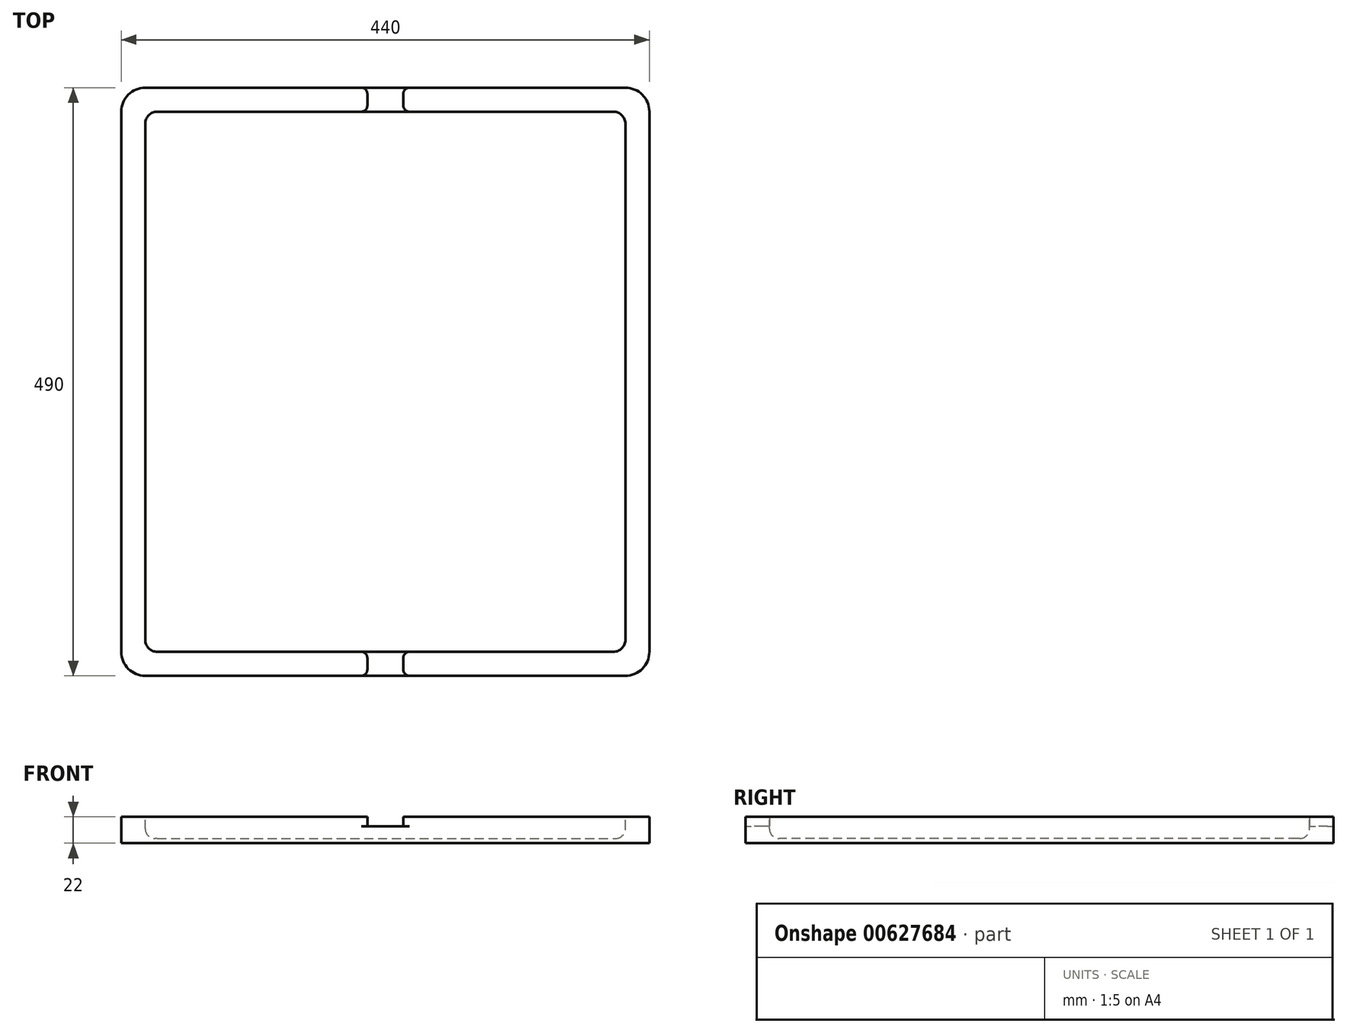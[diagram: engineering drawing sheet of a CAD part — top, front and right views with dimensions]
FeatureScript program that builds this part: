
annotation { "Feature Type Name" : "Feature", "Feature Type Description" : "" }
export const myFeature = defineFeature(function(context is Context, id is Id, definition is map)
    precondition{}
    {
        {
            var Q0;
            Q0=qCreatedBy(makeId("Top.planeOp"),FACE);
            var sketch = newSketch(context, id + "F0", { "sketchPlane" : qUnion([Q0])});
            skLineSegment(sketch, "E0", {"start": v(0, 245) * mm, "end": v(-200, 245) * mm});
            skLineSegment(sketch, "E1", {"start": v(-220, 225) * mm, "end": v(-220, 0) * mm});
            skArc(sketch, "E2", {"start": v(-200, 245) * mm, "mid": v(-214.14, 239.14) * mm, "end": v(-220, 225) * mm});
            skLineSegment(sketch, "E3.MirrorCS", {"start": v(220, 225) * mm, "end": v(220, 0) * mm});
            skArc(sketch, "E4.MirrorCS", {"start": v(200, 245) * mm, "mid": v(214.14, 239.14) * mm, "end": v(220, 225) * mm});
            skLineSegment(sketch, "E5.MirrorCS", {"start": v(0, 245) * mm, "end": v(200, 245) * mm});
            skLineSegment(sketch, "E6.MirrorCS", {"start": v(-220, -225) * mm, "end": v(-220, 0) * mm});
            skArc(sketch, "E7.MirrorCS", {"start": v(-200, -245) * mm, "mid": v(-214.14, -239.14) * mm, "end": v(-220, -225) * mm});
            skLineSegment(sketch, "E8.MirrorCS", {"start": v(0, -245) * mm, "end": v(-200, -245) * mm});
            skLineSegment(sketch, "E9.MirrorCS", {"start": v(0, -245) * mm, "end": v(200, -245) * mm});
            skArc(sketch, "E10.MirrorCS", {"start": v(200, -245) * mm, "mid": v(214.14, -239.14) * mm, "end": v(220, -225) * mm});
            skLineSegment(sketch, "E11.MirrorCS", {"start": v(220, -225) * mm, "end": v(220, 0) * mm});
            skSolve(sketch);
        }
        {
            var Q0;
            Q0=makeQuery(id+"F0.imprint","IMPRINT",FACE,{"disambiguationData":[TD([[makeQuery(id+"F0.imprint","IMPRINT",EDGE,{"derivedFrom":sQuery(id+"F0.wireOp",EDGE,"E0")}),1.0]])]});
            extrude(context, id + "F1", {"entities" : qUnion([Q0]), "depth" : 22 * mm, "offsetDistance" : 25 * mm});
        }
        {
            var Q0;
            Q0=makeQuery(id+"F1.opExtrude","CAP_FACE",FACE,{"disambiguationData":[OSD([sQuery(id+"F0.wireOp",EDGE,"E0"),sQuery(id+"F0.wireOp",EDGE,"E1"),sQuery(id+"F0.wireOp",EDGE,"E2"),sQuery(id+"F0.wireOp",EDGE,"E3.MirrorCS"),sQuery(id+"F0.wireOp",EDGE,"E4.MirrorCS"),sQuery(id+"F0.wireOp",EDGE,"E5.MirrorCS"),sQuery(id+"F0.wireOp",EDGE,"E6.MirrorCS"),sQuery(id+"F0.wireOp",EDGE,"E7.MirrorCS"),sQuery(id+"F0.wireOp",EDGE,"E8.MirrorCS"),sQuery(id+"F0.wireOp",EDGE,"E9.MirrorCS"),sQuery(id+"F0.wireOp",EDGE,"E10.MirrorCS"),sQuery(id+"F0.wireOp",EDGE,"E11.MirrorCS")])],"isStart":false});
            var sketch = newSketch(context, id + "F2", { "sketchPlane" : qUnion([Q0])});
            skLineSegment(sketch, "E12.bottom", {"start": v(-190, 225) * mm, "end": v(190, 225) * mm});
            skLineSegment(sketch, "E12.top", {"start": v(-190, -225) * mm, "end": v(190, -225) * mm});
            skLineSegment(sketch, "E12.left", {"start": v(-200, 215) * mm, "end": v(-200, -215) * mm});
            skLineSegment(sketch, "E12.right", {"start": v(200, 215) * mm, "end": v(200, -215) * mm});
            skPoint(sketch, "E13.visualSharp", {"position": v(200, -225) * mm});
            skArc(sketch, "E13.filletArc", {"start": v(190, -225) * mm, "mid": v(197.07, -222.07) * mm, "end": v(200, -215) * mm});
            skPoint(sketch, "E14.visualSharp", {"position": v(-200, -225) * mm});
            skArc(sketch, "E14.filletArc", {"start": v(-200, -215) * mm, "mid": v(-197.07, -222.07) * mm, "end": v(-190, -225) * mm});
            skPoint(sketch, "E15.visualSharp", {"position": v(-200, 225) * mm});
            skArc(sketch, "E15.filletArc", {"start": v(-190, 225) * mm, "mid": v(-197.07, 222.07) * mm, "end": v(-200, 215) * mm});
            skPoint(sketch, "E16.visualSharp", {"position": v(200, 225) * mm});
            skArc(sketch, "E16.filletArc", {"start": v(200, 215) * mm, "mid": v(197.07, 222.07) * mm, "end": v(190, 225) * mm});
            skSolve(sketch);
        }
        {
            var Q0;
            Q0=makeQuery(id+"F2.imprint","IMPRINT",FACE,{"disambiguationData":[TD([[makeQuery(id+"F2.imprint","IMPRINT",EDGE,{"derivedFrom":sQuery(id+"F2.wireOp",EDGE,"E12.bottom")}),-1.0]])]});
            extrude(context, id + "F3", {"entities" : qUnion([Q0]), "operationType" : NewBodyOperationType.REMOVE, "oppositeDirection" : true, "depth" : 18 * mm, "offsetDistance" : 25 * mm});
        }
        {
            var Q0;
            Q0=makeQuery(id+"F3.boolean.opBoolean","COPY",EDGE,{"derivedFrom":makeQuery(id+"F3.opExtrude","CAP_EDGE",EDGE,{"disambiguationData":[OSD([sQuery(id+"F2.wireOp",EDGE,"E12.bottom")])],"isStart":false})});
            var Q1;
            Q1=makeQuery(id+"F3.boolean.opBoolean","COPY",EDGE,{"derivedFrom":makeQuery(id+"F3.opExtrude","CAP_EDGE",EDGE,{"disambiguationData":[OSD([sQuery(id+"F2.wireOp",EDGE,"E15.filletArc")])],"isStart":false})});
            var Q2;
            Q2=makeQuery(id+"F3.boolean.opBoolean","COPY",FACE,{"derivedFrom":makeQuery(id+"F3.opExtrude","CAP_FACE",FACE,{"disambiguationData":[OSD([sQuery(id+"F2.wireOp",EDGE,"E12.bottom"),sQuery(id+"F2.wireOp",EDGE,"E12.top"),sQuery(id+"F2.wireOp",EDGE,"E12.left"),sQuery(id+"F2.wireOp",EDGE,"E12.right"),sQuery(id+"F2.wireOp",EDGE,"E13.filletArc"),sQuery(id+"F2.wireOp",EDGE,"E14.filletArc"),sQuery(id+"F2.wireOp",EDGE,"E15.filletArc"),sQuery(id+"F2.wireOp",EDGE,"E16.filletArc")])],"isStart":false})});
            fillet(context, id + "F4", {"entities" : qUnion([Q0, Q1, Q2]), "radius" : 8 * mm, "tangentPropagation" : true, "allowEdgeOverflow" : false});
        }
        {
            var Q0;
            Q0=makeQuery(id+"F1.opExtrude","CAP_FACE",FACE,{"disambiguationData":[OSD([sQuery(id+"F0.wireOp",EDGE,"E0"),sQuery(id+"F0.wireOp",EDGE,"E1"),sQuery(id+"F0.wireOp",EDGE,"E2"),sQuery(id+"F0.wireOp",EDGE,"E3.MirrorCS"),sQuery(id+"F0.wireOp",EDGE,"E4.MirrorCS"),sQuery(id+"F0.wireOp",EDGE,"E5.MirrorCS"),sQuery(id+"F0.wireOp",EDGE,"E6.MirrorCS"),sQuery(id+"F0.wireOp",EDGE,"E7.MirrorCS"),sQuery(id+"F0.wireOp",EDGE,"E8.MirrorCS"),sQuery(id+"F0.wireOp",EDGE,"E9.MirrorCS"),sQuery(id+"F0.wireOp",EDGE,"E10.MirrorCS"),sQuery(id+"F0.wireOp",EDGE,"E11.MirrorCS")])],"isStart":false});
            var sketch = newSketch(context, id + "F5", { "sketchPlane" : qUnion([Q0])});
            skLineSegment(sketch, "E17.bottom", {"start": v(-15, 290.14) * mm, "end": v(15, 290.14) * mm});
            skLineSegment(sketch, "E17.top", {"start": v(-15, -306.97) * mm, "end": v(15, -306.97) * mm});
            skLineSegment(sketch, "E17.left", {"start": v(-15, 290.14) * mm, "end": v(-15, -306.97) * mm});
            skLineSegment(sketch, "E17.right", {"start": v(15, 290.14) * mm, "end": v(15, -306.97) * mm});
            skSolve(sketch);
        }
        {
            var Q0;
            Q0 = qSketchRegion(id + "F5", true);
            extrude(context, id + "F6", {"entities" : qUnion([Q0]), "operationType" : NewBodyOperationType.REMOVE, "oppositeDirection" : true, "depth" : 8 * mm, "offsetDistance" : 25 * mm});
        }
        {
            var Q0;
            Q0=makeQuery(id+"F6.boolean.opBoolean","INTERSECT",EDGE,{"derivedFrom":[makeQuery(id+"F1.opExtrude","SWEPT_FACE",FACE,{"disambiguationData":[OSD([sQuery(id+"F0.wireOp",EDGE,"E8.MirrorCS"),sQuery(id+"F0.wireOp",EDGE,"E9.MirrorCS")])]}),makeQuery(id+"F6.opExtrude","SWEPT_FACE",FACE,{"disambiguationData":[OSD([sQuery(id+"F5.wireOp",EDGE,"E17.left")])]})]});
            var Q1;
            Q1=makeQuery(id+"F6.boolean.opBoolean","INTERSECT",EDGE,{"derivedFrom":[makeQuery(id+"F1.opExtrude","SWEPT_FACE",FACE,{"disambiguationData":[OSD([sQuery(id+"F0.wireOp",EDGE,"E8.MirrorCS"),sQuery(id+"F0.wireOp",EDGE,"E9.MirrorCS")])]}),makeQuery(id+"F6.opExtrude","SWEPT_FACE",FACE,{"disambiguationData":[OSD([sQuery(id+"F5.wireOp",EDGE,"E17.right")])]})]});
            var Q2;
            Q2=makeQuery(id+"F6.boolean.opBoolean","INTERSECT",EDGE,{"derivedFrom":[makeQuery(id+"F3.boolean.opBoolean","COPY",FACE,{"derivedFrom":makeQuery(id+"F3.opExtrude","SWEPT_FACE",FACE,{"disambiguationData":[OSD([sQuery(id+"F2.wireOp",EDGE,"E12.top")])]})}),makeQuery(id+"F6.opExtrude","SWEPT_FACE",FACE,{"disambiguationData":[OSD([sQuery(id+"F5.wireOp",EDGE,"E17.right")])]})]});
            var Q3;
            Q3=makeQuery(id+"F6.boolean.opBoolean","INTERSECT",EDGE,{"derivedFrom":[makeQuery(id+"F3.boolean.opBoolean","COPY",FACE,{"derivedFrom":makeQuery(id+"F3.opExtrude","SWEPT_FACE",FACE,{"disambiguationData":[OSD([sQuery(id+"F2.wireOp",EDGE,"E12.top")])]})}),makeQuery(id+"F6.opExtrude","SWEPT_FACE",FACE,{"disambiguationData":[OSD([sQuery(id+"F5.wireOp",EDGE,"E17.left")])]})]});
            var Q4;
            Q4=makeQuery(id+"F6.boolean.opBoolean","INTERSECT",EDGE,{"derivedFrom":[makeQuery(id+"F3.boolean.opBoolean","COPY",FACE,{"derivedFrom":makeQuery(id+"F3.opExtrude","SWEPT_FACE",FACE,{"disambiguationData":[OSD([sQuery(id+"F2.wireOp",EDGE,"E12.bottom")])]})}),makeQuery(id+"F6.opExtrude","SWEPT_FACE",FACE,{"disambiguationData":[OSD([sQuery(id+"F5.wireOp",EDGE,"E17.left")])]})]});
            var Q5;
            Q5=makeQuery(id+"F6.boolean.opBoolean","INTERSECT",EDGE,{"derivedFrom":[makeQuery(id+"F1.opExtrude","SWEPT_FACE",FACE,{"disambiguationData":[OSD([sQuery(id+"F0.wireOp",EDGE,"E0"),sQuery(id+"F0.wireOp",EDGE,"E5.MirrorCS")])]}),makeQuery(id+"F6.opExtrude","SWEPT_FACE",FACE,{"disambiguationData":[OSD([sQuery(id+"F5.wireOp",EDGE,"E17.left")])]})]});
            var Q6;
            Q6=makeQuery(id+"F6.boolean.opBoolean","INTERSECT",EDGE,{"derivedFrom":[makeQuery(id+"F3.boolean.opBoolean","COPY",FACE,{"derivedFrom":makeQuery(id+"F3.opExtrude","SWEPT_FACE",FACE,{"disambiguationData":[OSD([sQuery(id+"F2.wireOp",EDGE,"E12.bottom")])]})}),makeQuery(id+"F6.opExtrude","SWEPT_FACE",FACE,{"disambiguationData":[OSD([sQuery(id+"F5.wireOp",EDGE,"E17.right")])]})]});
            var Q7;
            Q7=makeQuery(id+"F6.boolean.opBoolean","INTERSECT",EDGE,{"derivedFrom":[makeQuery(id+"F1.opExtrude","SWEPT_FACE",FACE,{"disambiguationData":[OSD([sQuery(id+"F0.wireOp",EDGE,"E0"),sQuery(id+"F0.wireOp",EDGE,"E5.MirrorCS")])]}),makeQuery(id+"F6.opExtrude","SWEPT_FACE",FACE,{"disambiguationData":[OSD([sQuery(id+"F5.wireOp",EDGE,"E17.right")])]})]});
            fillet(context, id + "F7", {"entities" : qUnion([Q0, Q1, Q2, Q3, Q4, Q5, Q6, Q7]), "radius" : 5 * mm, "tangentPropagation" : true, "allowEdgeOverflow" : false});
        }
    });
